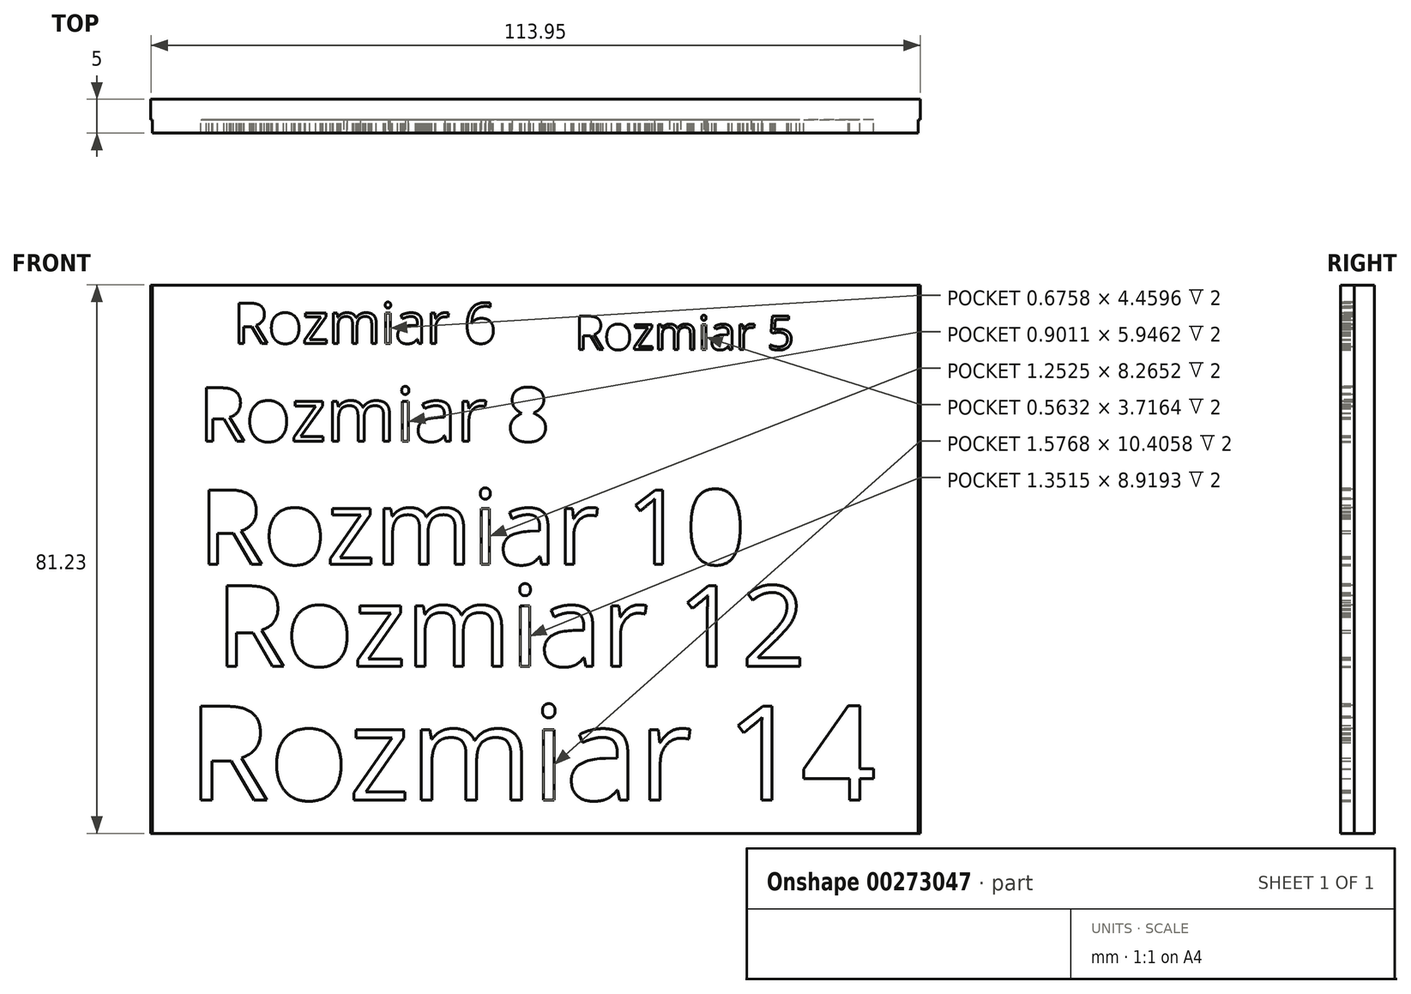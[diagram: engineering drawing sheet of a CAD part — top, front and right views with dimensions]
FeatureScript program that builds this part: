
annotation { "Feature Type Name" : "Feature", "Feature Type Description" : "" }
export const myFeature = defineFeature(function(context is Context, id is Id, definition is map)
    precondition{}
    {
        {
            var Q0;
            Q0=qCreatedBy(makeId("Front.planeOp"),FACE);
            var sketch = newSketch(context, id + "F0", { "sketchPlane" : qUnion([Q0])});
            skLineSegment(sketch, "E0.bottom", {"start": v(-51.07, 12.67) * mm, "end": v(62.38, 12.67) * mm});
            skLineSegment(sketch, "E0.top", {"start": v(-51.07, -68.56) * mm, "end": v(62.38, -68.56) * mm});
            skLineSegment(sketch, "E0.left", {"start": v(-51.07, 12.67) * mm, "end": v(-51.07, -68.56) * mm});
            skLineSegment(sketch, "E0.right", {"start": v(62.38, 12.67) * mm, "end": v(62.38, -68.56) * mm});
            skText(sketch, "E1", { "text": "Rozmiar 6", "fontName": "OpenSans-Regular.ttf"});
            skText(sketch, "E2", { "text": "Rozmiar 8", "fontName": "OpenSans-Regular.ttf"});
            skText(sketch, "E3", { "text": "Rozmiar 10", "fontName": "OpenSans-Regular.ttf"});
            skText(sketch, "E4", { "text": "Rozmiar 5", "fontName": "OpenSans-Regular.ttf"});
            skText(sketch, "E5", { "text": "Rozmiar 12", "fontName": "OpenSans-Regular.ttf"});
            skText(sketch, "E6", { "text": "Rozmiar 14", "fontName": "OpenSans-Regular.ttf"});
            const initialGuessF0  = {"E1": [-0.03904, 0.00403, 1, 0, 0.006], "E2": [-0.04411, -0.0105, 1, 0, 0.008], "E3": [-0.04416, -0.02872, 1, 0, 0.01112], "E4": [0.01155, 0.00309, 1, 0, 0.005], "E5": [-0.04163, -0.0438, 1, 0, 0.012], "E6": [-0.04575, -0.06362, 1, 0, 0.014]};
            skSetInitialGuess(sketch, initialGuessF0);
            skSolve(sketch);
        }
        {
            var Q0;
            Q0 = qSketchRegion(id + "F0", true);
            extrude(context, id + "F1", {"entities" : qUnion([Q0]), "depth" : 2 * mm});
        }
        {
            var Q0;
            Q0=qCreatedBy(makeId("Front.planeOp"),FACE);
            var sketch = newSketch(context, id + "F2", { "sketchPlane" : qUnion([Q0])});
            skLineSegment(sketch, "E7.bottom", {"start": v(-51.26, 12.66) * mm, "end": v(62.7, 12.66) * mm});
            skLineSegment(sketch, "E7.top", {"start": v(-51.26, -68.56) * mm, "end": v(62.7, -68.56) * mm});
            skLineSegment(sketch, "E7.left", {"start": v(-51.26, 12.66) * mm, "end": v(-51.26, -68.56) * mm});
            skLineSegment(sketch, "E7.right", {"start": v(62.7, 12.66) * mm, "end": v(62.7, -68.56) * mm});
            skSolve(sketch);
        }
        {
            var Q0;
            Q0 = qSketchRegion(id + "F2", true);
            extrude(context, id + "F3", {"entities" : qUnion([Q0]), "operationType" : NewBodyOperationType.ADD, "oppositeDirection" : true, "depth" : 3 * mm});
        }
    });
